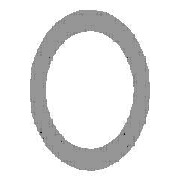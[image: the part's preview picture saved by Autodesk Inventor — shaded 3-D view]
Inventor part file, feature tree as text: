
AUTODESK INVENTOR PART (.ipt)
format: ipt  version: 2013 (Build 170138000, 138)  size: 114,176 bytes
history: native  units: mm (DEFAULTED — no unit token found)
features: other x4, sketch x3, plane x1
ambient origin geometry x8: Origin, YZ Plane, XZ Plane, XY Plane, X Axis, Y Axis, Z Axis, Center Point
bodies: Solid1 (feature_tree), Body (feature_tree)
feature tree (8):
  parser-record x1  (decoder bookkeeping rows leaked as tree rows — omitted from the tree; the rows remain in map.json)
  other  "Driven Length"
  other  "Start plane"
  other  "End plane"
  sketch  "Sketch"  dims[d2=76.2mm d3=0.0mm d4=-0.0mm d5=76.2mm d6=90.0deg d7=76.2mm]
  sketch  "Sketch3"  dims[d0=42.164mm]
  plane  "Work Plane3"
  sketch  "Sketch4"  dims[d1=3.556mm]
